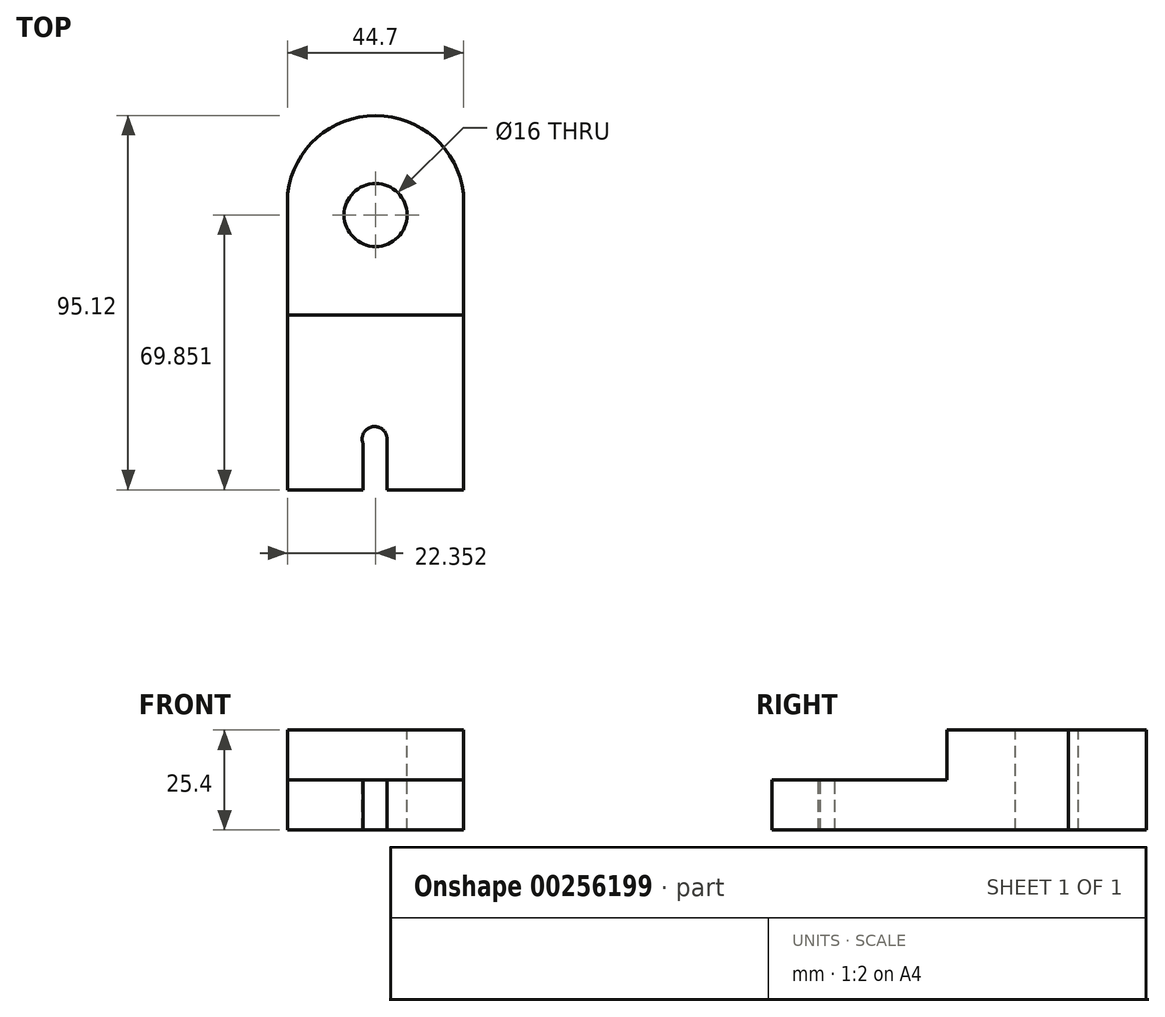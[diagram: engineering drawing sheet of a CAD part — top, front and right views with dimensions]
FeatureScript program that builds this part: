
annotation { "Feature Type Name" : "Feature", "Feature Type Description" : "" }
export const myFeature = defineFeature(function(context is Context, id is Id, definition is map)
    precondition{}
    {
        {
            var Q0;
            Q0=qCreatedBy(makeId("Right.planeOp"),FACE);
            var sketch = newSketch(context, id + "F0", { "sketchPlane" : qUnion([Q0])});
            skLineSegment(sketch, "E0", {"start": v(-33.48, 0) * mm, "end": v(61.77, 0) * mm});
            skLineSegment(sketch, "E1", {"start": v(61.77, 0) * mm, "end": v(61.77, 25.4) * mm});
            skLineSegment(sketch, "E2", {"start": v(61.77, 25.4) * mm, "end": v(10.97, 25.4) * mm});
            skLineSegment(sketch, "E3", {"start": v(10.97, 25.4) * mm, "end": v(10.97, 12.7) * mm});
            skLineSegment(sketch, "E4", {"start": v(10.97, 12.7) * mm, "end": v(-33.48, 12.7) * mm});
            skLineSegment(sketch, "E5", {"start": v(-33.48, 12.7) * mm, "end": v(-33.48, 0) * mm});
            skSolve(sketch);
        }
        {
            var Q0;
            Q0 = qSketchRegion(id + "F0", true);
            extrude(context, id + "F1", {"entities" : qUnion([Q0]), "depth" : 44.7 * mm});
        }
        {
            var Q0;
            Q0=makeQuery(id+"F1.opExtrude","SWEPT_FACE",FACE,{"disambiguationData":[OSD([sQuery(id+"F0.wireOp",EDGE,"E4")])]});
            var sketch = newSketch(context, id + "F2", { "sketchPlane" : qUnion([Q0])});
            skLineSegment(sketch, "E6", {"start": v(22.35, -33.48) * mm, "end": v(22.35, -20.78) * mm});
            skSolve(sketch);
        }
        {
            var Q0;
            {var subQ0=sQuery(id+"F0.wireOp",EDGE,"E4");var subQ1=makeQuery(id+"F1.opExtrude","CAP_EDGE",EDGE,{"disambiguationData":[OSD([subQ0])],"isStart":true});Q0=makeQuery(id+"F2.imprint","IMPRINT",FACE,{"disambiguationData":[TD([[makeQuery(id+"F2.imprint","IMPRINT",EDGE,{"derivedFrom":subQ1}),1.0]])]});}
            var sketch = newSketch(context, id + "F3", { "sketchPlane" : qUnion([Q0])});
            skLineSegment(sketch, "E7", {"start": v(15.74, -33.24) * mm, "end": v(15.74, -20.54) * mm});
            skLineSegment(sketch, "E8", {"start": v(15.74, -20.54) * mm, "end": v(28.44, -20.54) * mm});
            skLineSegment(sketch, "E9", {"start": v(28.44, -20.54) * mm, "end": v(28.44, -33.24) * mm});
            skCircle(sketch, "E10", {"center": v(22.1, -20.54) * mm, "radius": 6.17 * mm});
            skSolve(sketch);
        }
        {
            var Q0;
            Q0=sQuery(id+"F3.wireOp",VERTEX,"E10.center");
            var Q1;
            Q1=makeQuery(id+"F1.opExtrude","SWEPT_BODY",BODY,{"disambiguationData":[OSD([sQuery(id+"F0.wireOp",EDGE,"E0"),sQuery(id+"F0.wireOp",EDGE,"E1"),sQuery(id+"F0.wireOp",EDGE,"E2"),sQuery(id+"F0.wireOp",EDGE,"E3"),sQuery(id+"F0.wireOp",EDGE,"E4"),sQuery(id+"F0.wireOp",EDGE,"E5")])]});
            hole(context, id + "F4", {"style" : HoleStyle.SIMPLE, "endStyle" : HoleEndStyle.BLIND, "holeDiameter" : 6.35 * mm, "holeDepth" : 50.8 * mm, "isTappedThrough" : true, "tappedDepth" : 12.7 * mm, "tapClearance" : 3, "locations" : qUnion([Q0]), "scope" : qUnion([Q1])});
        }
        {
            var Q0;
            {var subQ0=sQuery(id+"F0.wireOp",EDGE,"E4");var subQ1=makeQuery(id+"F1.opExtrude","CAP_EDGE",EDGE,{"disambiguationData":[OSD([subQ0])],"isStart":true});Q0=makeQuery(id+"F2.imprint","IMPRINT",FACE,{"disambiguationData":[TD([[makeQuery(id+"F2.imprint","IMPRINT",EDGE,{"derivedFrom":subQ1}),1.0]])]});}
            var sketch = newSketch(context, id + "F5", { "sketchPlane" : qUnion([Q0])});
            skLineSegment(sketch, "E11", {"start": v(19.1, -21.06) * mm, "end": v(19.1, -33.98) * mm});
            skLineSegment(sketch, "E12", {"start": v(19.1, -21.06) * mm, "end": v(25.3, -21.06) * mm});
            skLineSegment(sketch, "E13", {"start": v(25.3, -21.06) * mm, "end": v(25.3, -33.76) * mm});
            skLineSegment(sketch, "E14", {"start": v(19.1, -33.98) * mm, "end": v(25.3, -33.76) * mm});
            skSolve(sketch);
        }
        {
            var Q0;
            Q0 = qSketchRegion(id + "F5", true);
            extrude(context, id + "F6", {"entities" : qUnion([Q0]), "operationType" : NewBodyOperationType.REMOVE, "oppositeDirection" : true, "depth" : 25.4 * mm});
        }
        {
            var Q0;
            Q0=makeQuery(id+"F1.opExtrude","SWEPT_FACE",FACE,{"disambiguationData":[OSD([sQuery(id+"F0.wireOp",EDGE,"E2")])]});
            var sketch = newSketch(context, id + "F7", { "sketchPlane" : qUnion([Q0])});
            skArc(sketch, "E15", {"start": v(44.7, 36.37) * mm, "mid": v(22.35, 61.64) * mm, "end": v(0, 36.37) * mm});
            skSolve(sketch);
        }
        {
            var Q0;
            {var subQ1=sQuery(id+"F0.wireOp",EDGE,"E2");var subQ6=makeQuery(id+"F1.opExtrude","SWEPT_EDGE",EDGE,{"disambiguationData":[OSD([sQuery(id+"F0.wireOp",EDGE,"E1"),subQ1])]});Q0=makeQuery(id+"F7.imprint","IMPRINT",FACE,{"disambiguationData":[TD([[makeQuery(id+"F7.imprint","IMPRINT",EDGE,{"derivedFrom":subQ6}),1.0]])]});}
            extrude(context, id + "F8", {"entities" : qUnion([Q0]), "operationType" : NewBodyOperationType.REMOVE, "oppositeDirection" : true, "depth" : 25.4 * mm});
        }
        {
            var Q0;
            Q0=makeQuery(id+"F1.opExtrude","SWEPT_FACE",FACE,{"disambiguationData":[OSD([sQuery(id+"F0.wireOp",EDGE,"E2")])]});
            var sketch = newSketch(context, id + "F9", { "sketchPlane" : qUnion([Q0])});
            skLineSegment(sketch, "E16", {"start": v(22.35, 10.97) * mm, "end": v(22.35, 36.37) * mm});
            skCircle(sketch, "E17", {"center": v(22.35, 36.37) * mm, "radius": 8 * mm});
            skSolve(sketch);
        }
        {
            var Q0;
            Q0=makeQuery(id+"F9.imprint","IMPRINT",FACE,{"disambiguationData":[TD([[makeQuery(id+"F9.imprint","IMPRINT",EDGE,{"derivedFrom":sQuery(id+"F9.wireOp",EDGE,"E17")}),1.0]])]});
            extrude(context, id + "F10", {"entities" : qUnion([Q0]), "operationType" : NewBodyOperationType.REMOVE, "oppositeDirection" : true, "depth" : 25.4 * mm});
        }
    });
